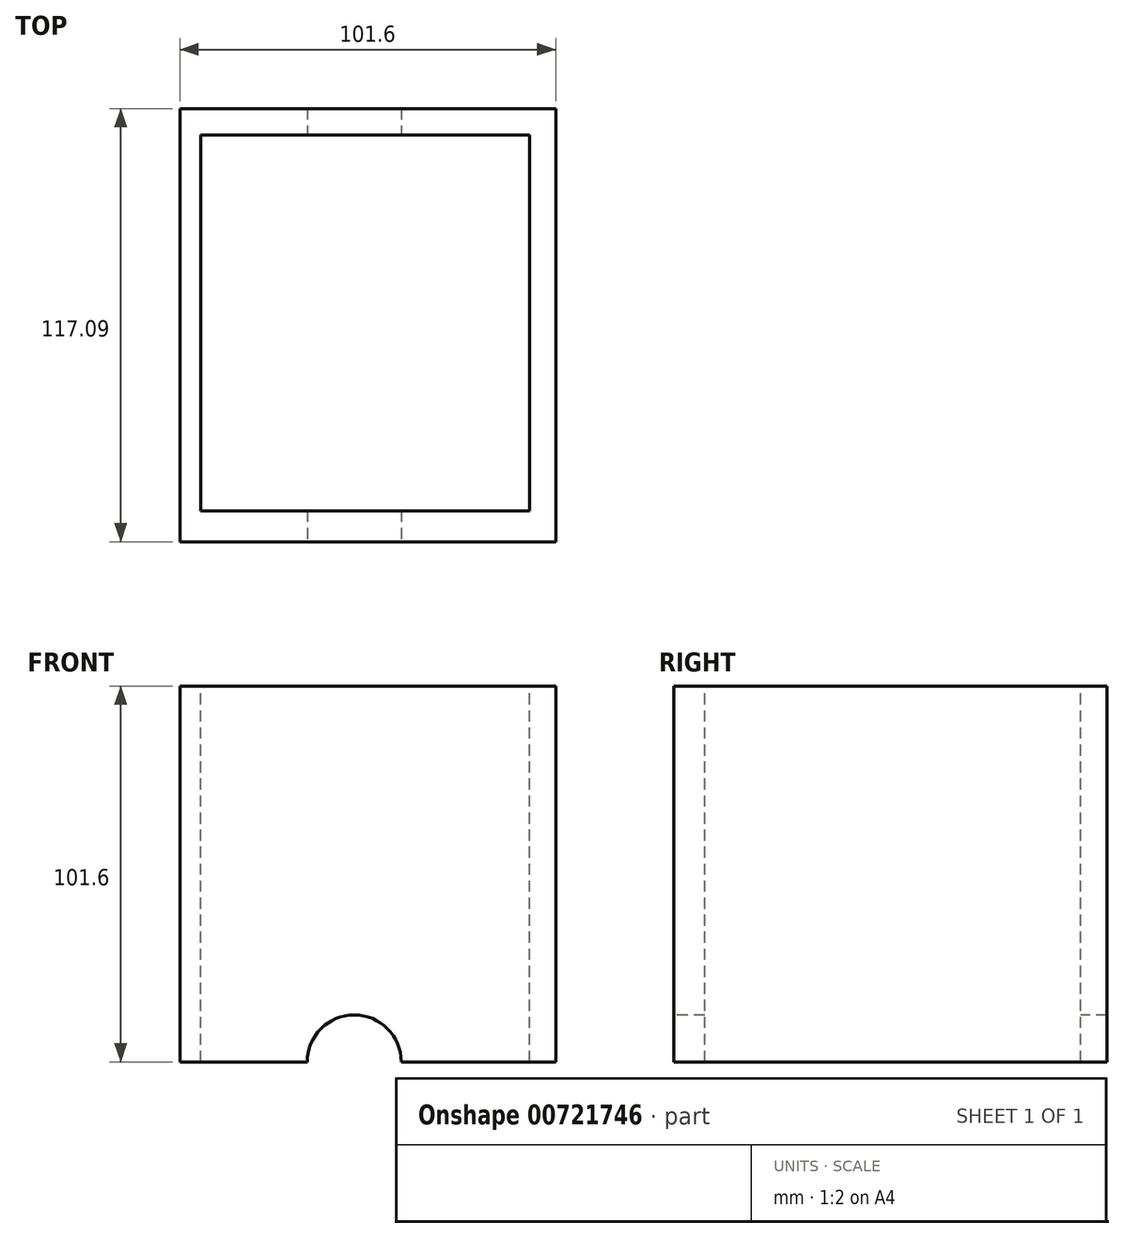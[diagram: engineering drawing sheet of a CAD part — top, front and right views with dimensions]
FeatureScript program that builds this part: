
annotation { "Feature Type Name" : "Feature", "Feature Type Description" : "" }
export const myFeature = defineFeature(function(context is Context, id is Id, definition is map)
    precondition{}
    {
        {
            var Q0;
            Q0=qCreatedBy(makeId("Front.planeOp"),FACE);
            var sketch = newSketch(context, id + "F0", { "sketchPlane" : qUnion([Q0])});
            skLineSegment(sketch, "E0", {"start": v(0, 0) * mm, "end": v(0, 101.6) * mm});
            skLineSegment(sketch, "E1", {"start": v(0, 101.6) * mm, "end": v(101.6, 101.6) * mm});
            skLineSegment(sketch, "E2", {"start": v(101.6, 101.6) * mm, "end": v(101.6, 0) * mm});
            skLineSegment(sketch, "E3", {"start": v(0, 0) * mm, "end": v(101.6, 0) * mm});
            skSolve(sketch);
        }
        {
            var Q0;
            Q0=makeQuery(id+"F0.imprint","IMPRINT",FACE,{"disambiguationData":[TD([[makeQuery(id+"F0.imprint","IMPRINT",EDGE,{"derivedFrom":sQuery(id+"F0.wireOp",EDGE,"E0")}),-1.0]])]});
            var sketch = newSketch(context, id + "F1", { "sketchPlane" : qUnion([Q0])});
            skArc(sketch, "E4", {"start": v(59.83, 0) * mm, "mid": v(47.13, 12.7) * mm, "end": v(34.43, 0) * mm});
            skLineSegment(sketch, "E5", {"start": v(34.43, 0) * mm, "end": v(59.83, 0) * mm});
            skSolve(sketch);
        }
        {
            var Q0;
            Q0=makeQuery(id+"F0.imprint","IMPRINT",FACE,{"disambiguationData":[TD([[makeQuery(id+"F0.imprint","IMPRINT",EDGE,{"derivedFrom":sQuery(id+"F0.wireOp",EDGE,"E0")}),-1.0]])]});
            extrude(context, id + "F2", {"entities" : qUnion([Q0]), "oppositeDirection" : true, "depth" : 117.1 * mm, "offsetDistance" : 25.4 * mm});
        }
        {
            var Q0;
            Q0 = qSketchRegion(id + "F1", true);
            extrude(context, id + "F3", {"entities" : qUnion([Q0]), "operationType" : NewBodyOperationType.REMOVE, "oppositeDirection" : true, "depth" : 117.1 * mm, "offsetDistance" : 25.4 * mm});
        }
        {
            var Q0;
            Q0=makeQuery(id+"F2.opExtrude","SWEPT_FACE",FACE,{"disambiguationData":[OSD([sQuery(id+"F0.wireOp",EDGE,"E1")])]});
            var sketch = newSketch(context, id + "F4", { "sketchPlane" : qUnion([Q0])});
            skLineSegment(sketch, "E6", {"start": v(5.6, 109.95) * mm, "end": v(5.6, 8.35) * mm});
            skLineSegment(sketch, "E7", {"start": v(5.6, 8.35) * mm, "end": v(94.5, 8.35) * mm});
            skLineSegment(sketch, "E8", {"start": v(94.5, 109.95) * mm, "end": v(5.6, 109.95) * mm});
            skLineSegment(sketch, "E9", {"start": v(94.5, 109.95) * mm, "end": v(94.5, 8.35) * mm});
            skSolve(sketch);
        }
        {
            var Q0;
            Q0=makeQuery(id+"F4.imprint","IMPRINT",FACE,{"disambiguationData":[TD([[makeQuery(id+"F4.imprint","IMPRINT",EDGE,{"derivedFrom":sQuery(id+"F4.wireOp",EDGE,"E6")}),1.0]])]});
            extrude(context, id + "F5", {"entities" : qUnion([Q0]), "operationType" : NewBodyOperationType.REMOVE, "oppositeDirection" : true, "depth" : 104.4 * mm, "offsetDistance" : 25.4 * mm});
        }
    });
